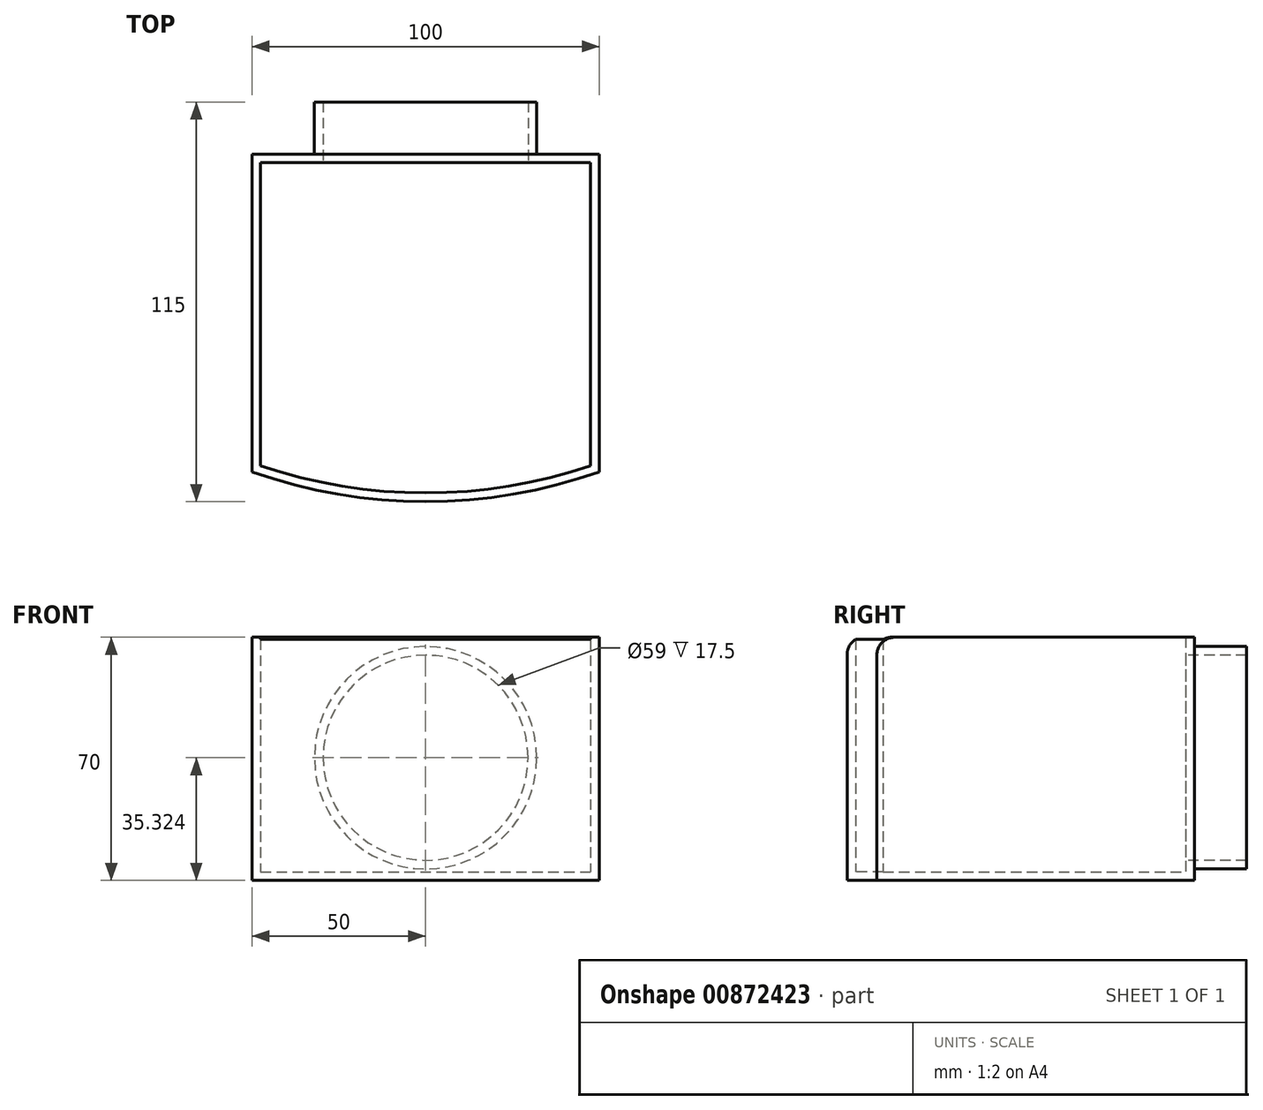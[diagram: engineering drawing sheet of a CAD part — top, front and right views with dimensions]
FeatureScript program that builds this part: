
annotation { "Feature Type Name" : "Feature", "Feature Type Description" : "" }
export const myFeature = defineFeature(function(context is Context, id is Id, definition is map)
    precondition{}
    {
        {
            var Q0;
            Q0=qCreatedBy(makeId("Top.planeOp"),FACE);
            var sketch = newSketch(context, id + "F0", { "sketchPlane" : qUnion([Q0])});
            skLineSegment(sketch, "E0", {"start": v(0, -150) * mm, "end": v(-50, -150) * mm});
            skLineSegment(sketch, "E1", {"start": v(0, -150) * mm, "end": v(50, -150) * mm});
            skLineSegment(sketch, "E2", {"start": v(50, -150) * mm, "end": v(50, -50) * mm});
            skLineSegment(sketch, "E3", {"start": v(-50, -50) * mm, "end": v(-50, -150) * mm});
            skCircle(sketch, "E4", {"center": v(0, 0) * mm, "radius": 150 * mm});
            skLineSegment(sketch, "E5", {"start": v(0, -50) * mm, "end": v(50, -50) * mm});
            skPoint(sketch, "E6.end.orphan", {"position": v(50, 0) * mm});
            skLineSegment(sketch, "E7", {"start": v(0, -50) * mm, "end": v(-50, -50) * mm});
            skPoint(sketch, "E8.end.orphan", {"position": v(-50, 0) * mm});
            skSolve(sketch);
        }
        {
            var Q0;
            {var subQ7=sQuery(id+"F0.wireOp",EDGE,"E5");Q0=makeQuery(id+"F0.imprint","IMPRINT",FACE,{"disambiguationData":[TD([[makeQuery(id+"F0.imprint","IMPRINT",EDGE,{"derivedFrom":subQ7}),-1.0]])]});}
            extrude(context, id + "F1", {"entities" : qUnion([Q0]), "depth" : 70 * mm, "offsetDistance" : 25 * mm});
        }
        {
            var Q0;
            Q0=makeQuery(id+"F1.opExtrude","CAP_FACE",FACE,{"disambiguationData":[OSD([sQuery(id+"F0.wireOp",EDGE,"E2"),sQuery(id+"F0.wireOp",EDGE,"E3"),sQuery(id+"F0.wireOp",EDGE,"E4"),sQuery(id+"F0.wireOp",EDGE,"E5"),sQuery(id+"F0.wireOp",EDGE,"E7")])],"isStart":false});
            shell(context, id + "F2", {"entities" : qUnion([Q0]), "thickness" : 2.5 * mm});
        }
        {
            var Q0;
            Q0=makeQuery(id+"F1.opExtrude","CAP_EDGE",EDGE,{"disambiguationData":[OSD([sQuery(id+"F0.wireOp",EDGE,"E4")])],"isStart":false});
            fillet(context, id + "F3", {"entities" : qUnion([Q0]), "radius" : 5 * mm, "tangentPropagation" : true, "allowEdgeOverflow" : false});
        }
        {
            var Q0;
            Q0=makeQuery(id+"F1.opExtrude","SWEPT_FACE",FACE,{"disambiguationData":[OSD([sQuery(id+"F0.wireOp",EDGE,"E5"),sQuery(id+"F0.wireOp",EDGE,"E7")])]});
            var sketch = newSketch(context, id + "F4", { "sketchPlane" : qUnion([Q0])});
            skLineSegment(sketch, "E9", {"start": v(0, 0) * mm, "end": v(0, 35.32) * mm});
            skCircle(sketch, "E10", {"center": v(0, 35.32) * mm, "radius": 32 * mm});
            skSolve(sketch);
        }
        {
            var Q0;
            Q0=makeQuery(id+"F4.imprint","IMPRINT",FACE,{"disambiguationData":[TD([[makeQuery(id+"F4.imprint","IMPRINT",EDGE,{"derivedFrom":sQuery(id+"F4.wireOp",EDGE,"E10")}),1.0]])]});
            extrude(context, id + "F5", {"entities" : qUnion([Q0]), "operationType" : NewBodyOperationType.ADD, "depth" : 15 * mm, "offsetDistance" : 25 * mm});
        }
        {
            var Q0;
            Q0=makeQuery(id+"F5.opExtrude","CAP_FACE",FACE,{"disambiguationData":[OSD([sQuery(id+"F4.wireOp",EDGE,"E10")])],"isStart":false});
            shell(context, id + "F6", {"entities" : qUnion([Q0]), "thickness" : 2.5 * mm});
        }
        {
            var Q0;
            Q0=makeQuery(id+"F6.opShell","OFFSET_FACE",FACE,{"disambiguationData":[OSD([sQuery(id+"F0.wireOp",EDGE,"E5"),sQuery(id+"F0.wireOp",EDGE,"E7")])]});
            extrude(context, id + "F7", {"entities" : qUnion([Q0]), "operationType" : NewBodyOperationType.REMOVE, "oppositeDirection" : true, "depth" : 25 * mm, "offsetDistance" : 25 * mm});
        }
    });
